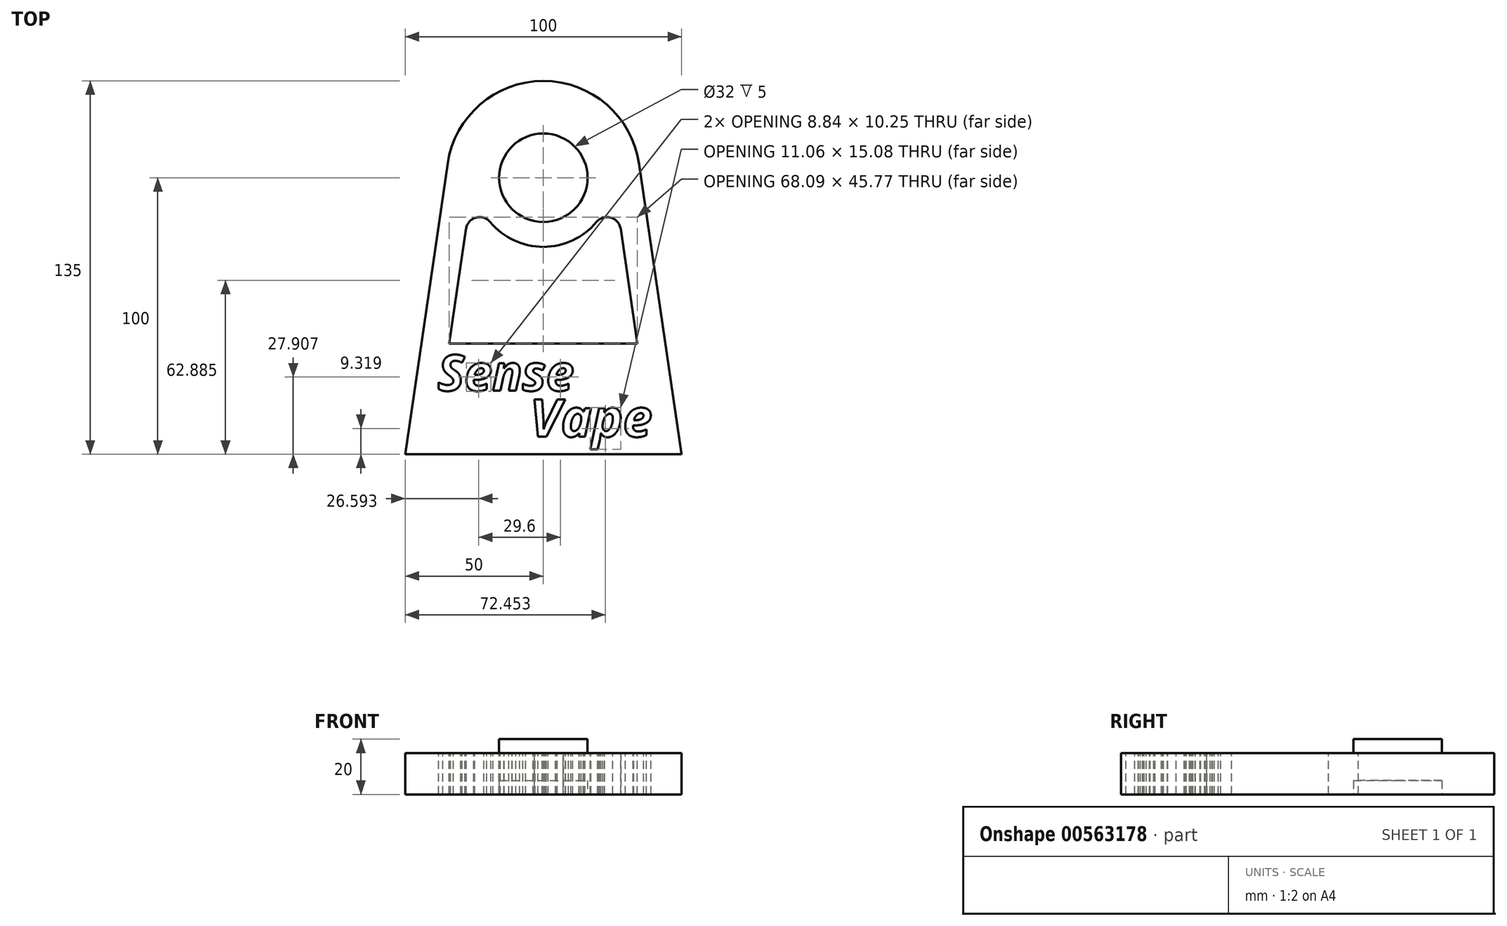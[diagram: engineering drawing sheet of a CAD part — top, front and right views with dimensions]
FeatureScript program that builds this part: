
annotation { "Feature Type Name" : "Feature", "Feature Type Description" : "" }
export const myFeature = defineFeature(function(context is Context, id is Id, definition is map)
    precondition{}
    {
        {
            var Q0;
            Q0=qCreatedBy(makeId("Top.planeOp"),FACE);
            var sketch = newSketch(context, id + "F0", { "sketchPlane" : qUnion([Q0])});
            skLineSegment(sketch, "E0", {"start": v(-50, -100) * mm, "end": v(-34.63, 5.07) * mm});
            skLineSegment(sketch, "E1", {"start": v(34.63, 5.07) * mm, "end": v(50, -100) * mm});
            skLineSegment(sketch, "E2", {"start": v(-50, -100) * mm, "end": v(50, -100) * mm});
            skArc(sketch, "E3", {"start": v(-34.63, 5.07) * mm, "mid": v(0, 35) * mm, "end": v(34.63, 5.07) * mm});
            skLineSegment(sketch, "E4", {"start": v(-34.63, 5.07) * mm, "end": v(0, 241.82) * mm, "construction": true});
            skLineSegment(sketch, "E5", {"start": v(0, 241.82) * mm, "end": v(34.63, 5.07) * mm, "construction": true});
            skSolve(sketch);
        }
        {
            var Q0;
            Q0 = qSketchRegion(id + "F0", true);
            extrude(context, id + "F1", {"entities" : qUnion([Q0]), "depth" : 15 * mm, "offsetDistance" : 25 * mm});
        }
        {
            var Q0;
            Q0=makeQuery(id+"F1.opExtrude","CAP_FACE",FACE,{"disambiguationData":[OSD([sQuery(id+"F0.wireOp",EDGE,"E0"),sQuery(id+"F0.wireOp",EDGE,"E1"),sQuery(id+"F0.wireOp",EDGE,"E2"),sQuery(id+"F0.wireOp",EDGE,"E3")])],"isStart":false});
            var sketch = newSketch(context, id + "F2", { "sketchPlane" : qUnion([Q0])});
            skCircle(sketch, "E6", {"center": v(0, 0) * mm, "radius": 16 * mm});
            skSolve(sketch);
        }
        {
            var Q0;
            Q0 = qSketchRegion(id + "F2", true);
            extrude(context, id + "F3", {"entities" : qUnion([Q0]), "operationType" : NewBodyOperationType.ADD, "depth" : 5 * mm, "offsetDistance" : 25 * mm});
        }
        {
            var Q0;
            Q0=makeQuery(id+"F1.opExtrude","CAP_FACE",FACE,{"disambiguationData":[OSD([sQuery(id+"F0.wireOp",EDGE,"E0"),sQuery(id+"F0.wireOp",EDGE,"E1"),sQuery(id+"F0.wireOp",EDGE,"E2"),sQuery(id+"F0.wireOp",EDGE,"E3")])],"isStart":true});
            var sketch = newSketch(context, id + "F4", { "sketchPlane" : qUnion([Q0])});
            skCircle(sketch, "E7", {"center": v(0, 0) * mm, "radius": 16 * mm});
            skSolve(sketch);
        }
        {
            var Q0;
            Q0 = qSketchRegion(id + "F4", true);
            extrude(context, id + "F5", {"entities" : qUnion([Q0]), "operationType" : NewBodyOperationType.REMOVE, "oppositeDirection" : true, "depth" : 5 * mm, "offsetDistance" : 25 * mm});
        }
        {
            var Q0;
            {var subQ0=sQuery(id+"F0.wireOp",EDGE,"E3");var subQ1=sQuery(id+"F0.wireOp",EDGE,"E2");var subQ2=sQuery(id+"F0.wireOp",EDGE,"E0");var subQ3=sQuery(id+"F0.wireOp",EDGE,"E1");Q0=makeQuery(id+"F5MRjXVDiMk5iRC_1.boolean.opBoolean","SPLIT",FACE,{"disambiguationData":[TD([makeQuery(id+"F1.opExtrude","SWEPT_FACE",FACE,{"disambiguationData":[OSD([subQ2])]})])],"derivedFrom":makeQuery(id+"F1.opExtrude","CAP_FACE",FACE,{"disambiguationData":[OSD([subQ2,subQ3,subQ1,subQ0])],"isStart":false})});}
            var sketch = newSketch(context, id + "F6", { "sketchPlane" : qUnion([Q0])});
            skLineSegment(sketch, "E8", {"start": v(-34.04, -60) * mm, "end": v(34.04, -60) * mm});
            skLineSegment(sketch, "E9", {"start": v(34.04, -60) * mm, "end": v(27.97, -18.5) * mm});
            skLineSegment(sketch, "E10", {"start": v(-34.04, -60) * mm, "end": v(-27.97, -18.5) * mm});
            skArc(sketch, "E11", {"start": v(-19.19, -16.03) * mm, "mid": v(0, -25) * mm, "end": v(19.19, -16.03) * mm});
            skArc(sketch, "E12.filletArc", {"start": v(-19.19, -16.03) * mm, "mid": v(-24.38, -14.42) * mm, "end": v(-27.97, -18.5) * mm});
            skArc(sketch, "E13.filletArc", {"start": v(27.97, -18.5) * mm, "mid": v(24.38, -14.42) * mm, "end": v(19.19, -16.03) * mm});
            skSolve(sketch);
        }
        {
            var Q0;
            Q0 = qSketchRegion(id + "F6", true);
            extrude(context, id + "F7", {"entities" : qUnion([Q0]), "operationType" : NewBodyOperationType.REMOVE, "endBound" : BoundingType.THROUGH_ALL, "oppositeDirection" : true, "depth" : 25 * mm, "offsetDistance" : 25 * mm});
        }
        {
            var Q0;
            Q0=makeQuery(id+"F1.opExtrude","CAP_FACE",FACE,{"disambiguationData":[OSD([sQuery(id+"F0.wireOp",EDGE,"E0"),sQuery(id+"F0.wireOp",EDGE,"E1"),sQuery(id+"F0.wireOp",EDGE,"E2"),sQuery(id+"F0.wireOp",EDGE,"E3")])],"isStart":false});
            var sketch = newSketch(context, id + "F8", { "sketchPlane" : qUnion([Q0])});
            skText(sketch, "E14", { "text": "Sense", "fontName": "OpenSans-BoldItalic.ttf"});
            skText(sketch, "E15", { "text": "Vape", "fontName": "OpenSans-BoldItalic.ttf"});
            const initialGuessF8  = {"E14": [-0.03822, -0.07704, 1, 0, 0.01304], "E15": [-0.00486, -0.09367, 1, 0, 0.01363]};
            skSetInitialGuess(sketch, initialGuessF8);
            skSolve(sketch);
        }
        {
            var Q0;
            Q0 = qSketchRegion(id + "F8", true);
            extrude(context, id + "F9", {"entities" : qUnion([Q0]), "operationType" : NewBodyOperationType.REMOVE, "endBound" : BoundingType.THROUGH_ALL, "oppositeDirection" : true, "depth" : 25 * mm, "offsetDistance" : 25 * mm});
        }
    });
